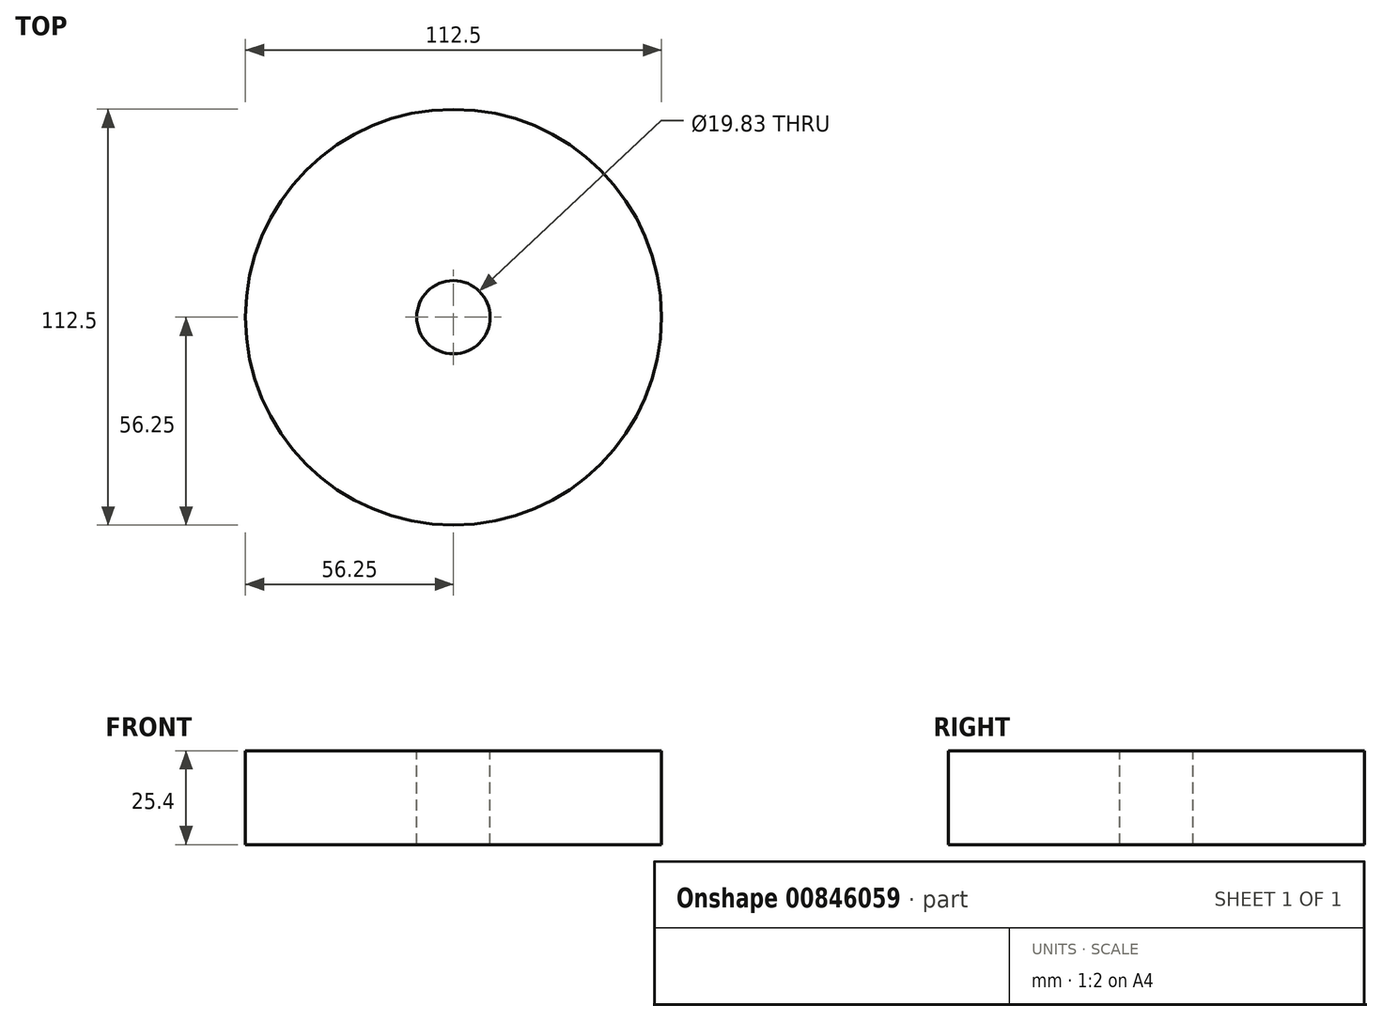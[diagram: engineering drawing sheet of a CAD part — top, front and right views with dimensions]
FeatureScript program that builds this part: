
annotation { "Feature Type Name" : "Feature", "Feature Type Description" : "" }
export const myFeature = defineFeature(function(context is Context, id is Id, definition is map)
    precondition{}
    {
        {
            var Q0;
            Q0=qCreatedBy(makeId("Top.planeOp"),FACE);
            var sketch = newSketch(context, id + "F0", { "sketchPlane" : qUnion([Q0])});
            skCircle(sketch, "E0", {"center": v(0, 0) * mm, "radius": 56.25 * mm});
            skSolve(sketch);
        }
        {
            var Q0;
            Q0 = qSketchRegion(id + "F0", true);
            extrude(context, id + "F1", {"entities" : qUnion([Q0]), "depth" : 25.4 * mm, "offsetDistance" : 25.4 * mm});
        }
        {
            var Q0;
            Q0=qCreatedBy(makeId("Top.planeOp"),FACE);
            var sketch = newSketch(context, id + "F2", { "sketchPlane" : qUnion([Q0])});
            skCircle(sketch, "E1", {"center": v(0, 0) * mm, "radius": 9.92 * mm});
            skSolve(sketch);
        }
        {
            var Q0;
            Q0 = qSketchRegion(id + "F2", true);
            extrude(context, id + "F3", {"entities" : qUnion([Q0]), "operationType" : NewBodyOperationType.REMOVE, "endBound" : BoundingType.THROUGH_ALL, "oppositeDirection" : true, "depth" : 25.4 * mm, "offsetDistance" : 25.4 * mm, "hasSecondDirection" : true, "secondDirectionOppositeDirection" : false, "secondDirectionDepth" : 25.4 * mm});
        }
    });
